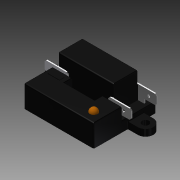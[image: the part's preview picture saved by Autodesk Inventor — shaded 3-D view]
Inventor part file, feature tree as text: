
AUTODESK INVENTOR PART (.ipt)
format: ipt  version: 2014 SP1 (Build 180222100, 222)  size: 413,696 bytes
history: native  units: mm (DEFAULTED — no unit token found)
features: sketch x3, fillet x2, plane x2, extrude x2, other x1, hole x1, mirror x1, imported_body x1
ambient origin geometry x8: Origin, YZ Plane, XZ Plane, XY Plane, X Axis, Y Axis, Z Axis, Center Point
bodies: Solid1 (feature_tree)
feature tree (13):
  other  "Spike Relay.ipt"
  fillet  "Fillet1"  Radius=0.762mm
  sketch  "Sketch2"  dims[d14=13.208mm d15=29.083mm]
  plane  "Work Plane1"
  extrude  "Extrusion1"  Depth=29.083mm
  extrude  "Extrusion2"  Depth=25.4mm TaperAngle=0.0deg
  hole  "Hole1"  [1 undecoded]
  plane  "Work Plane2"
  mirror  "Mirror2"
  fillet  "Fillet2"  [1 undecoded]
  imported_body  "DerivedBody::Spike Relay.ipt"
  sketch  "Sketch3"  dims[d16=34.0868mm d17=-4.318mm d18=25.4mm d19=0.0mm]
  sketch  "Sketch4"  dims[d20=25.4mm d21=0.0mm d22=4.4958mm d23=19.05mm d24=8.4328mm d25=6.35mm d26=14.3117mm d27=25.4mm d28=20.594885mm d29=0.635mm]
note: 2 required parameter values undecoded (feature->parameter linkage not recoverable at this tier; creation-order binding heuristic only, values carry confidence <= 0.55)
